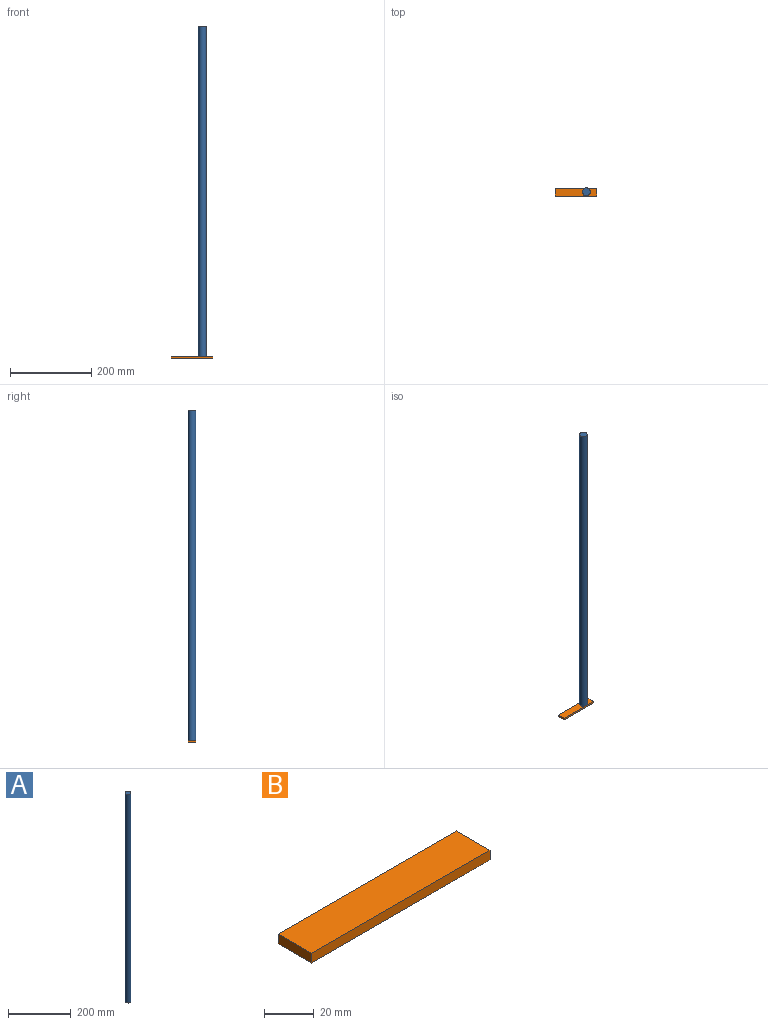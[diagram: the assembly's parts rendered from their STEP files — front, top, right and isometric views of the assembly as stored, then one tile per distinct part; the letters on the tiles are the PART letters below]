
ASSEMBLY  parts=2 mates=1
PART A: 3 faces, bbox 19.1x19.1x812.8 mm
  f0: cylinder r=9.53mm len=812.8mm, axis (0,0,-1), area 48643.9mm2, adj f1,f2
  f1: plane 19.05x19.05mm, normal (0,0,1), area 285mm2, adj f0
  f2: plane 19.05x19.05mm, normal (0,0,-1), area 285mm2, adj f0
PART B: 6 faces, bbox 101.6x19.1x4.8 mm
  f0: plane 19.05x4.76mm, normal (-1,0,0), area 90.7mm2, adj f1,f3,f4,f5
  f1: plane 101.6x4.76mm, normal (0,-1,0), area 483.9mm2, adj f0,f2,f4,f5
  f2: plane 19.05x4.76mm, normal (1,0,0), area 90.7mm2, adj f1,f3,f4,f5
  f3: plane 101.6x4.76mm, normal (0,1,0), area 483.9mm2, adj f0,f2,f4,f5
  f4: plane 101.6x19.05mm, normal (0,0,1), area 1935.5mm2, adj f0,f1,f2,f3
  f5: plane 101.6x19.05mm, normal (0,0,-1), area 1935.5mm2, adj f0,f1,f2,f3
PLACE A t=(-436.52,13.44,72.09)mm
PLACE B t=(-468.75,-38.8,67.33)mm
MATE fastened A.f0 <-> B.f4  axis (0,0,-1) through (-436.52,13.44,72.09)mm
